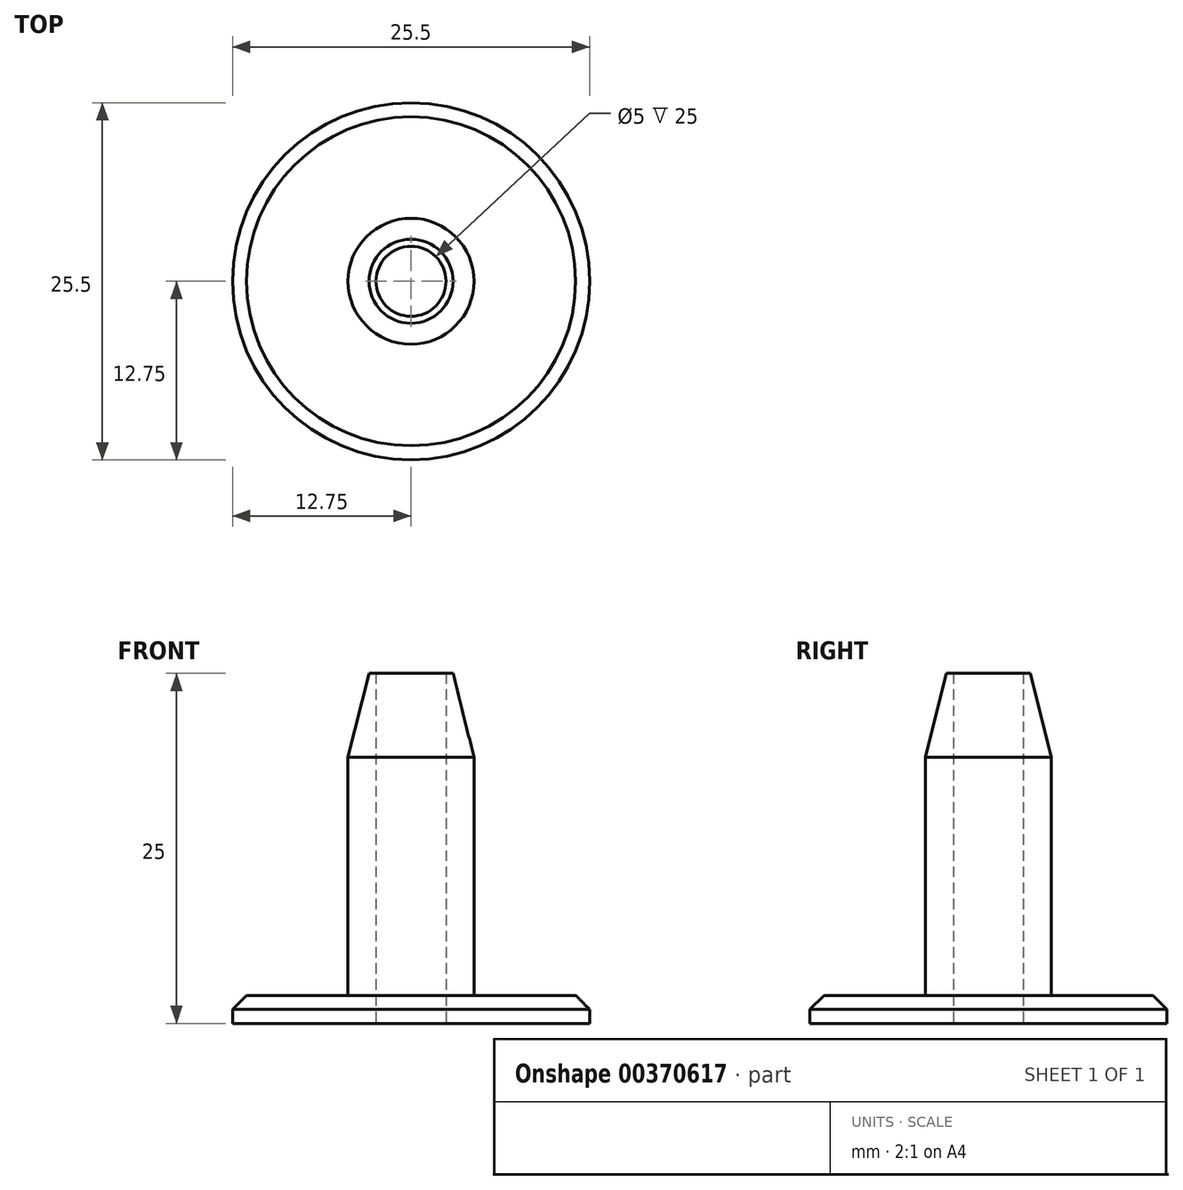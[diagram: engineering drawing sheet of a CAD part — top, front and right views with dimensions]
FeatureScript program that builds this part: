
annotation { "Feature Type Name" : "Feature", "Feature Type Description" : "" }
export const myFeature = defineFeature(function(context is Context, id is Id, definition is map)
    precondition{}
    {
        {
            var Q0;
            Q0=qCreatedBy(makeId("Top.planeOp"),FACE);
            var sketch = newSketch(context, id + "F0", { "sketchPlane" : qUnion([Q0])});
            skCircle(sketch, "E0", {"center": v(0, 0) * mm, "radius": 12.75 * mm});
            skCircle(sketch, "E1", {"center": v(0, 0) * mm, "radius": 4.5 * mm});
            skSolve(sketch);
        }
        {
            var Q0;
            Q0=makeQuery(id+"F0.imprint","IMPRINT",FACE,{"disambiguationData":[TD([[makeQuery(id+"F0.imprint","IMPRINT",EDGE,{"derivedFrom":sQuery(id+"F0.wireOp",EDGE,"E1")}),1.0]])]});
            extrude(context, id + "F1", {"entities" : qUnion([Q0]), "depth" : 25 * mm});
        }
        {
            var Q0;
            Q0=makeQuery(id+"F0.imprint","IMPRINT",FACE,{"disambiguationData":[TD([[makeQuery(id+"F0.imprint","IMPRINT",EDGE,{"derivedFrom":sQuery(id+"F0.wireOp",EDGE,"E0")}),1.0]])]});
            extrude(context, id + "F2", {"entities" : qUnion([Q0]), "operationType" : NewBodyOperationType.ADD, "depth" : 2 * mm});
        }
        {
            var Q0;
            Q0=makeQuery(id+"F1.opExtrude","CAP_EDGE",EDGE,{"disambiguationData":[OSD([sQuery(id+"F0.wireOp",EDGE,"E1")])],"isStart":false});
            chamfer(context, id + "F3", {"entities" : qUnion([Q0]), "chamferType" : ChamferType.TWO_OFFSETS, "width1" : 1.5 * mm, "oppositeDirection" : false, "width2" : 6 * mm, "tangentPropagation" : true});
        }
        {
            var Q0;
            Q0=sQuery(id+"F0.wireOp",VERTEX,"E0.center");
            var Q1;
            Q1=makeQuery(id+"F1.opExtrude","SWEPT_BODY",BODY,{"disambiguationData":[OSD([sQuery(id+"F0.wireOp",EDGE,"E1")])]});
            hole(context, id + "F4", {"style" : HoleStyle.SIMPLE, "endStyle" : HoleEndStyle.THROUGH, "oppositeDirection" : true, "holeDiameter" : 5 * mm, "isTappedThrough" : true, "tappedDepth" : 12 * mm, "tapClearance" : 3, "locations" : qUnion([Q0]), "scope" : qUnion([Q1])});
        }
        {
            var Q0;
            Q0=makeQuery(id+"F2.opExtrude","CAP_EDGE",EDGE,{"disambiguationData":[OSD([sQuery(id+"F0.wireOp",EDGE,"E0")])],"isStart":false});
            chamfer(context, id + "F5", {"entities" : qUnion([Q0]), "chamferType" : ChamferType.TWO_OFFSETS, "width1" : 1 * mm, "oppositeDirection" : false, "width2" : 1 * mm, "tangentPropagation" : true});
        }
    });
